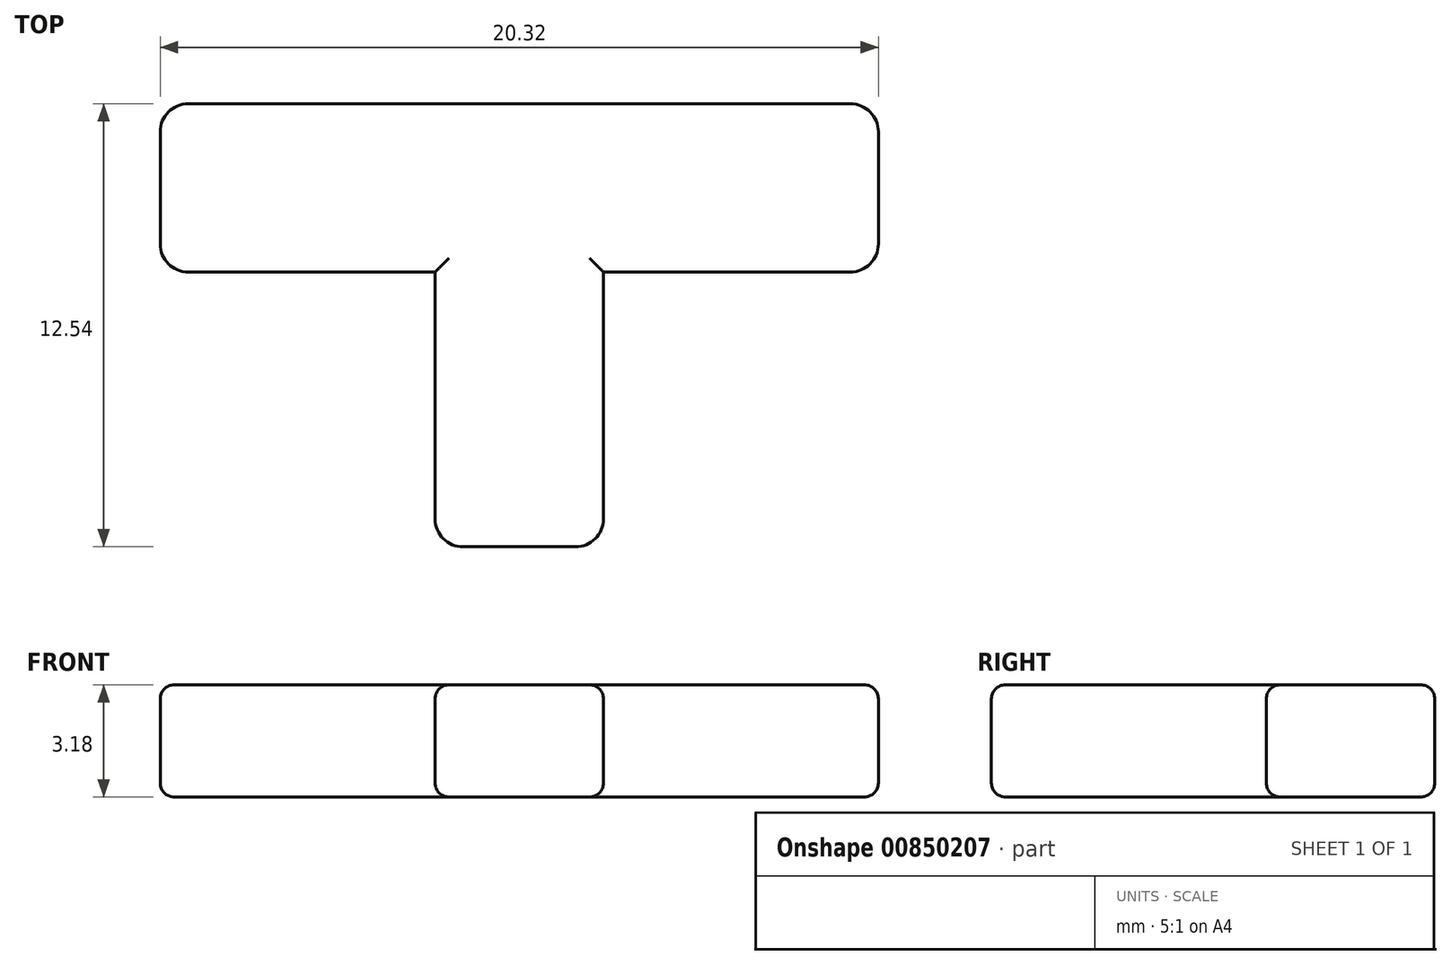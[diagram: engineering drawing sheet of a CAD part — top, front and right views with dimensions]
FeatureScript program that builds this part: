
annotation { "Feature Type Name" : "Feature", "Feature Type Description" : "" }
export const myFeature = defineFeature(function(context is Context, id is Id, definition is map)
    precondition{}
    {
        {
            var Q0;
            Q0=qCreatedBy(makeId("Top.planeOp"),FACE);
            var sketch = newSketch(context, id + "F0", { "sketchPlane" : qUnion([Q0])});
            skLineSegment(sketch, "E0.top", {"start": v(1.59, -10.16) * mm, "end": v(-1.59, -10.16) * mm});
            skLineSegment(sketch, "E0.left", {"start": v(2.38, 2.38) * mm, "end": v(2.38, -9.37) * mm});
            skLineSegment(sketch, "E0.right", {"start": v(-2.38, 2.38) * mm, "end": v(-2.38, -9.37) * mm});
            skPoint(sketch, "E0.middle", {"position": v(0, 0) * mm});
            skLineSegment(sketch, "E1.bottom", {"start": v(9.37, 2.38) * mm, "end": v(-9.37, 2.38) * mm});
            skLineSegment(sketch, "E1.top", {"start": v(9.37, -2.38) * mm, "end": v(-9.37, -2.38) * mm});
            skLineSegment(sketch, "E1.left", {"start": v(10.16, 1.59) * mm, "end": v(10.16, -1.59) * mm});
            skLineSegment(sketch, "E1.right", {"start": v(-10.16, 1.59) * mm, "end": v(-10.16, -1.59) * mm});
            skPoint(sketch, "E2.visualSharp", {"position": v(10.16, 2.38) * mm});
            skArc(sketch, "E2.filletArc", {"start": v(10.16, 1.59) * mm, "mid": v(9.93, 2.15) * mm, "end": v(9.37, 2.38) * mm});
            skPoint(sketch, "E3.visualSharp", {"position": v(10.16, -2.38) * mm});
            skArc(sketch, "E3.filletArc", {"start": v(9.37, -2.38) * mm, "mid": v(9.93, -2.15) * mm, "end": v(10.16, -1.59) * mm});
            skPoint(sketch, "E4.visualSharp", {"position": v(2.38, -10.16) * mm});
            skArc(sketch, "E4.filletArc", {"start": v(1.59, -10.16) * mm, "mid": v(2.15, -9.93) * mm, "end": v(2.38, -9.37) * mm});
            skPoint(sketch, "E5.visualSharp", {"position": v(-2.38, -10.16) * mm});
            skArc(sketch, "E5.filletArc", {"start": v(-2.38, -9.37) * mm, "mid": v(-2.15, -9.93) * mm, "end": v(-1.59, -10.16) * mm});
            skPoint(sketch, "E6.visualSharp", {"position": v(-10.16, -2.38) * mm});
            skArc(sketch, "E6.filletArc", {"start": v(-10.16, -1.59) * mm, "mid": v(-9.93, -2.15) * mm, "end": v(-9.37, -2.38) * mm});
            skPoint(sketch, "E7.visualSharp", {"position": v(-10.16, 2.38) * mm});
            skArc(sketch, "E7.filletArc", {"start": v(-9.37, 2.38) * mm, "mid": v(-9.93, 2.15) * mm, "end": v(-10.16, 1.59) * mm});
            skSolve(sketch);
        }
        {
            var Q0;
            Q0 = qSketchRegion(id + "F0", true);
            extrude(context, id + "F1", {"entities" : qUnion([Q0]), "depth" : 3.17 * mm, "offsetDistance" : 25.4 * mm});
        }
        {
            var Q0;
            Q0=makeQuery(id+"F1.opExtrude","CAP_FACE",FACE,{"disambiguationData":[OSD([sQuery(id+"F0.wireOp",EDGE,"E0.bottom"),sQuery(id+"F0.wireOp",EDGE,"E0.top"),sQuery(id+"F0.wireOp",EDGE,"E0.left"),sQuery(id+"F0.wireOp",EDGE,"E0.right"),sQuery(id+"F0.wireOp",EDGE,"E1.bottom"),sQuery(id+"F0.wireOp",EDGE,"E1.top"),sQuery(id+"F0.wireOp",EDGE,"E1.left"),sQuery(id+"F0.wireOp",EDGE,"E1.right"),sQuery(id+"F0.wireOp",EDGE,"e48c8cea-de37-4d7b-bebe-fad5d6120350.filletArc"),sQuery(id+"F0.wireOp",EDGE,"ac0e0184-b8f9-40ee-be1f-0dbaa781b01f.filletArc"),sQuery(id+"F0.wireOp",EDGE,"E2.filletArc"),sQuery(id+"F0.wireOp",EDGE,"E3.filletArc"),sQuery(id+"F0.wireOp",EDGE,"E4.filletArc"),sQuery(id+"F0.wireOp",EDGE,"E5.filletArc"),sQuery(id+"F0.wireOp",EDGE,"E6.filletArc"),sQuery(id+"F0.wireOp",EDGE,"E7.filletArc")])],"isStart":false});
            var Q1;
            Q1=makeQuery(id+"F1.opExtrude","CAP_FACE",FACE,{"disambiguationData":[OSD([sQuery(id+"F0.wireOp",EDGE,"E0.bottom"),sQuery(id+"F0.wireOp",EDGE,"E0.top"),sQuery(id+"F0.wireOp",EDGE,"E0.left"),sQuery(id+"F0.wireOp",EDGE,"E0.right"),sQuery(id+"F0.wireOp",EDGE,"E1.bottom"),sQuery(id+"F0.wireOp",EDGE,"E1.top"),sQuery(id+"F0.wireOp",EDGE,"E1.left"),sQuery(id+"F0.wireOp",EDGE,"E1.right"),sQuery(id+"F0.wireOp",EDGE,"e48c8cea-de37-4d7b-bebe-fad5d6120350.filletArc"),sQuery(id+"F0.wireOp",EDGE,"ac0e0184-b8f9-40ee-be1f-0dbaa781b01f.filletArc"),sQuery(id+"F0.wireOp",EDGE,"E2.filletArc"),sQuery(id+"F0.wireOp",EDGE,"E3.filletArc"),sQuery(id+"F0.wireOp",EDGE,"E4.filletArc"),sQuery(id+"F0.wireOp",EDGE,"E5.filletArc"),sQuery(id+"F0.wireOp",EDGE,"E6.filletArc"),sQuery(id+"F0.wireOp",EDGE,"E7.filletArc")])],"isStart":true});
            fillet(context, id + "F2", {"entities" : qUnion([Q0, Q1]), "tangentPropagation" : true, "radius" : 0.4 * mm, "defaultsChanged" : false, "vertexSettings" : [], "allowEdgeOverflow" : false});
        }
    });
